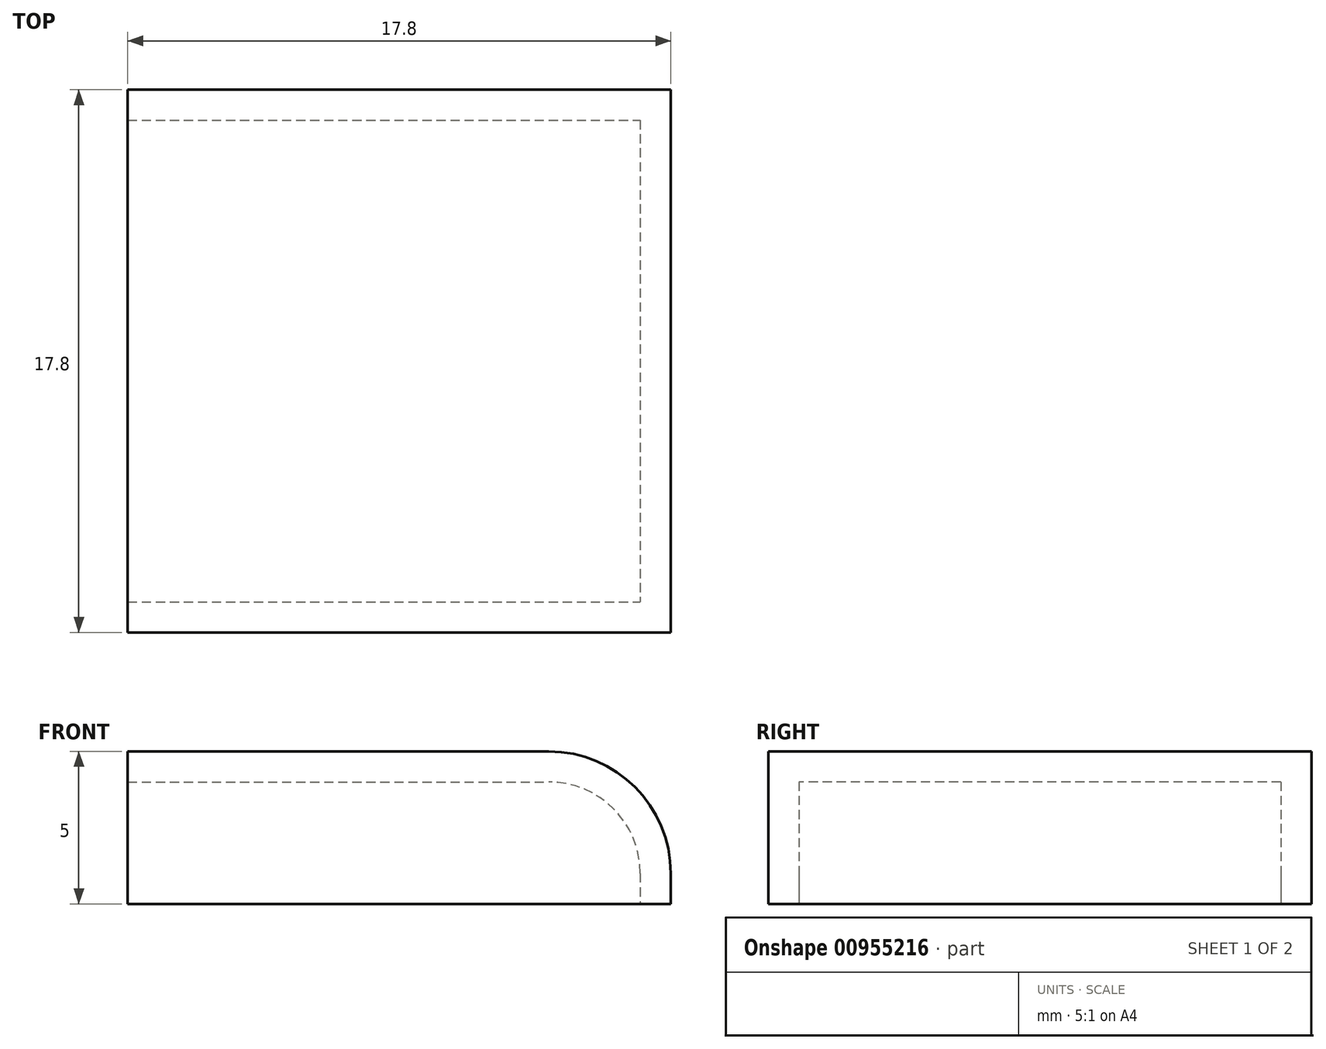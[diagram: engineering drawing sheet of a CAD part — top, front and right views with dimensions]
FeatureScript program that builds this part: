
annotation { "Feature Type Name" : "Feature", "Feature Type Description" : "" }
export const myFeature = defineFeature(function(context is Context, id is Id, definition is map)
    precondition{}
    {
        {
            var Q0;
            Q0=qCreatedBy(makeId("Top.planeOp"),FACE);
            var sketch = newSketch(context, id + "F0", { "sketchPlane" : qUnion([Q0])});
            skLineSegment(sketch, "E0.bottom", {"start": v(-17.8, 17.8) * mm, "end": v(0, 17.8) * mm});
            skLineSegment(sketch, "E0.top", {"start": v(-17.8, 0) * mm, "end": v(0, 0) * mm});
            skLineSegment(sketch, "E0.left", {"start": v(-17.8, 17.8) * mm, "end": v(-17.8, 0) * mm});
            skLineSegment(sketch, "E0.right", {"start": v(0, 17.8) * mm, "end": v(0, 0) * mm});
            skSolve(sketch);
        }
        {
            var Q0;
            Q0 = qSketchRegion(id + "F0", true);
            extrude(context, id + "F1", {"entities" : qUnion([Q0]), "depth" : 5 * mm, "offsetDistance" : 25 * mm});
        }
        {
            var Q0;
            Q0=makeQuery(id+"F1.opExtrude","CAP_EDGE",EDGE,{"disambiguationData":[OSD([sQuery(id+"F0.wireOp",EDGE,"E0.right")])],"isStart":false});
            fillet(context, id + "F2", {"entities" : qUnion([Q0]), "radius" : 4 * mm, "tangentPropagation" : true, "allowEdgeOverflow" : false});
        }
        {
            var Q0;
            Q0=makeQuery(id+"F1.opExtrude","CAP_FACE",FACE,{"disambiguationData":[OSD([sQuery(id+"F0.wireOp",EDGE,"E0.bottom"),sQuery(id+"F0.wireOp",EDGE,"E0.top"),sQuery(id+"F0.wireOp",EDGE,"E0.left"),sQuery(id+"F0.wireOp",EDGE,"E0.right")])],"isStart":true});
            var Q1;
            Q1=makeQuery(id+"F1.opExtrude","SWEPT_FACE",FACE,{"disambiguationData":[OSD([sQuery(id+"F0.wireOp",EDGE,"E0.left")])]});
            shell(context, id + "F3", {"entities" : qUnion([Q0, Q1]), "thickness" : 1 * mm});
        }
    });
